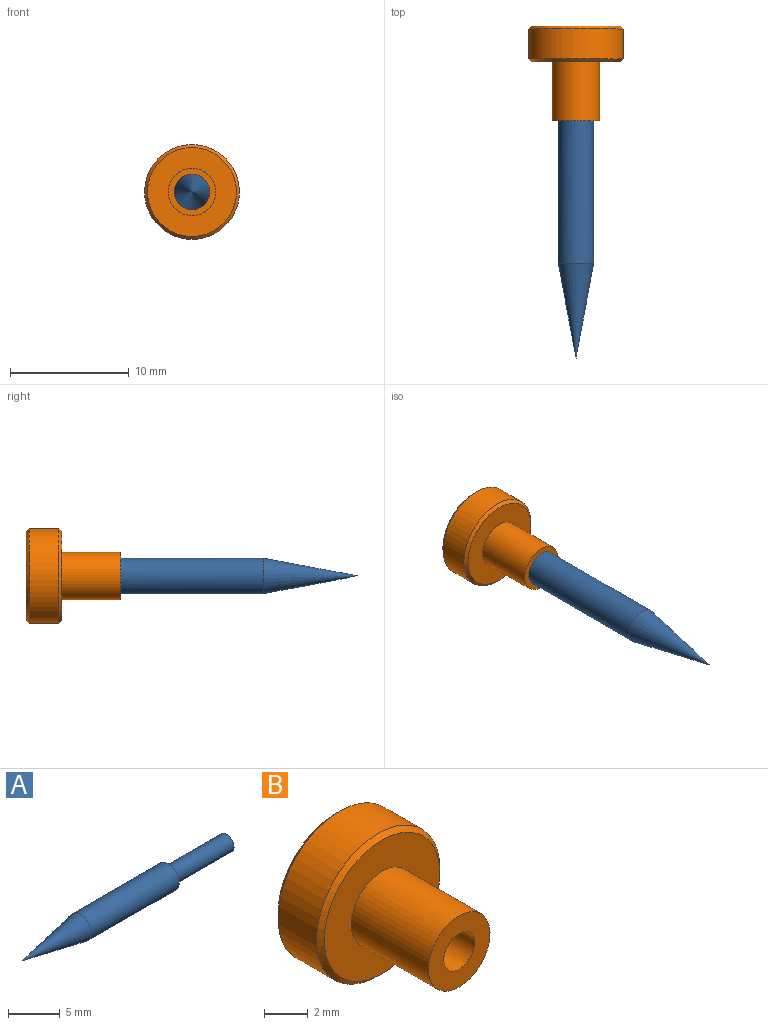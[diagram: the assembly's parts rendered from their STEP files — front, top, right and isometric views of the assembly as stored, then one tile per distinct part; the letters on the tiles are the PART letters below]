
ASSEMBLY  parts=2 mates=1
PART A: 5 faces, bbox 28x3x3 mm
  f0: plane 3x3mm, normal (1,0,0), area 3.9mm2, adj f1,f4
  f1: cylinder r=1.5mm len=12mm, axis (-1,0,0), area 113.1mm2, adj f0,f2
  f2: cone r=1.5mm half-angle=10.6deg, axis (1,0,0), area 38.4mm2, adj f1
  f3: plane 2x2mm, normal (1,0,0), area 3.1mm2, adj f4
  f4: cylinder r=1mm len=8mm, axis (-1,0,0), area 50.3mm2, adj f0,f3
PART B: 8 faces, bbox 8x8x8 mm
  f0: cylinder r=4mm len=8mm, axis (0,1,0), area 62.8mm2, adj f6,f7
  f1: plane 7.5x7.5mm, normal (0,-1,0), area 31.6mm2, adj f3,f7
  f2: plane 7.5x7.5mm, normal (0,1,0), area 41mm2, adj f5,f6
  f3: cylinder r=2mm len=5mm, axis (0,1,0), area 62.8mm2, adj f1,f4
  f4: plane 4x4mm, normal (0,-1,0), area 9.4mm2, adj f3,f5
  f5: cylinder r=1mm len=8mm, axis (0,-1,0), area 50.3mm2, adj f2,f4
  f6: cone r=4mm half-angle=45deg, axis (0,-1,0), area 8.6mm2, adj f0,f2
  f7: cone r=3.75mm half-angle=45deg, axis (0,1,0), area 8.6mm2, adj f0,f1
PLACE A rot(axis=(0.71,0.71,0),180deg) t=(-2.97,-29.8,-3.44)mm
PLACE B t=(-2.97,-12.01,-3.44)mm
MATE fastened A.f1 <-> B.f5  axis (0,-1,0) through (-2.97,-12.01,-3.44)mm
